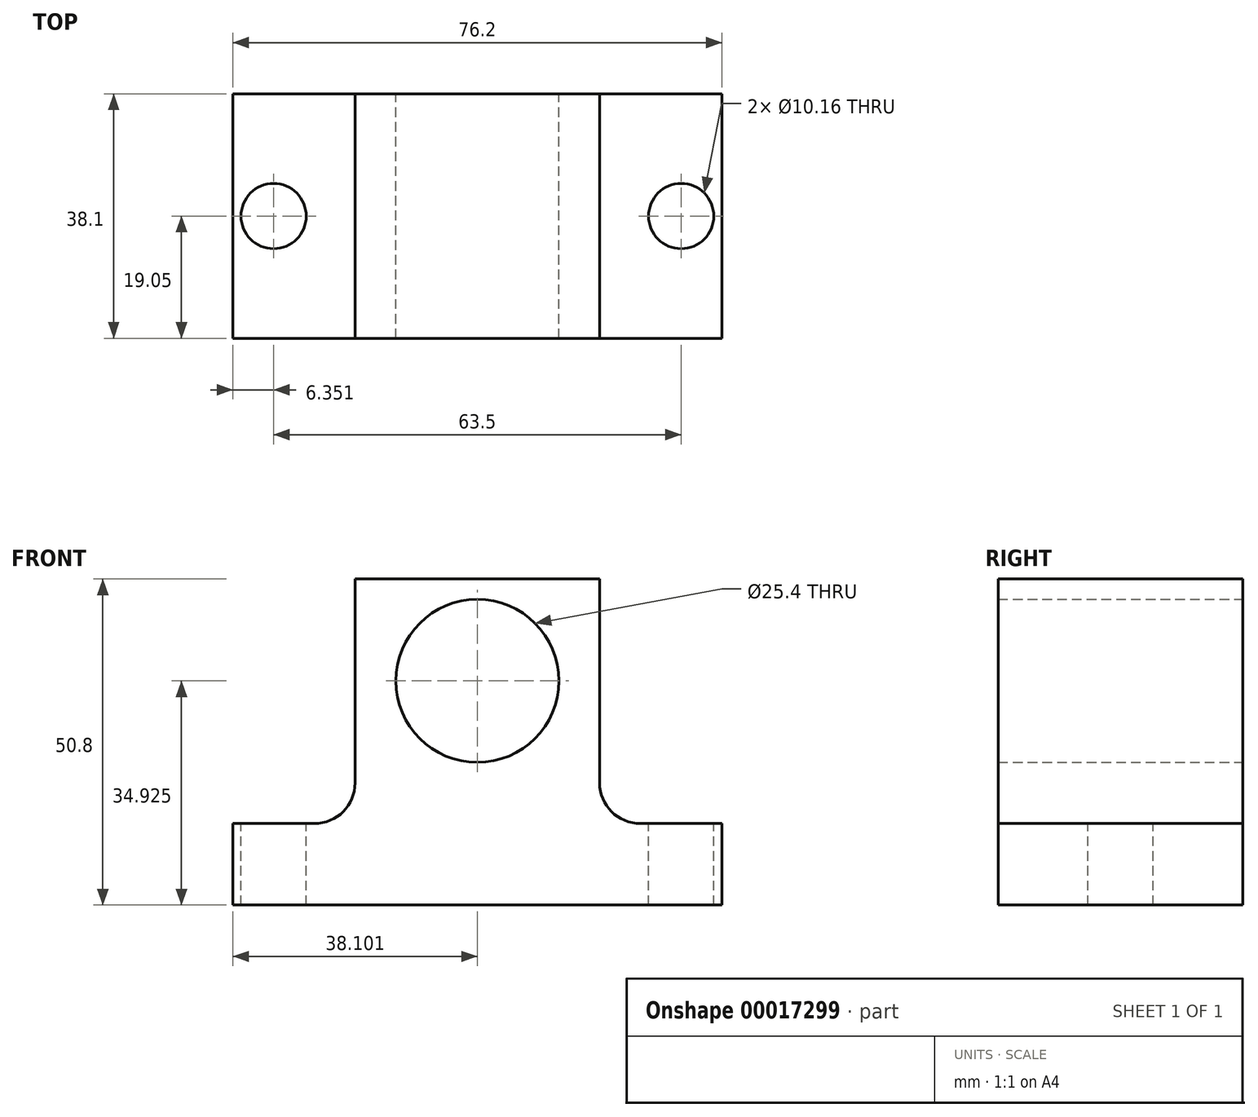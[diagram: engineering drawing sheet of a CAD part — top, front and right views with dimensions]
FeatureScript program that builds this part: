
annotation { "Feature Type Name" : "Feature", "Feature Type Description" : "" }
export const myFeature = defineFeature(function(context is Context, id is Id, definition is map)
    precondition{}
    {
        {
            var Q0;
            Q0=qCreatedBy(makeId("Front.planeOp"),FACE);
            var sketch = newSketch(context, id + "F0", { "sketchPlane" : qUnion([Q0])});
            skLineSegment(sketch, "E0", {"start": v(-55.57, 0) * mm, "end": v(-55.57, -12.7) * mm});
            skLineSegment(sketch, "E1", {"start": v(1.58, 6.35) * mm, "end": v(1.58, 38.1) * mm});
            skLineSegment(sketch, "E2", {"start": v(1.58, 38.1) * mm, "end": v(-36.52, 38.1) * mm});
            skLineSegment(sketch, "E3", {"start": v(20.63, 0) * mm, "end": v(20.63, -12.7) * mm});
            skLineSegment(sketch, "E4", {"start": v(7.93, 0) * mm, "end": v(20.63, 0) * mm});
            skLineSegment(sketch, "E5", {"start": v(20.63, -12.7) * mm, "end": v(-55.57, -12.7) * mm});
            skPoint(sketch, "E6.visualSharp", {"position": v(1.58, 0) * mm});
            skArc(sketch, "E6.filletArc", {"start": v(1.58, 6.35) * mm, "mid": v(3.44, 1.86) * mm, "end": v(7.93, 0) * mm});
            skLineSegment(sketch, "E7", {"start": v(-36.52, 38.1) * mm, "end": v(-36.52, 6.35) * mm});
            skLineSegment(sketch, "E8", {"start": v(-55.57, 0) * mm, "end": v(-42.87, 0) * mm});
            skPoint(sketch, "E9.visualSharp", {"position": v(-36.52, 0) * mm});
            skArc(sketch, "E9.filletArc", {"start": v(-42.87, 0) * mm, "mid": v(-38.38, 1.86) * mm, "end": v(-36.52, 6.35) * mm});
            skCircle(sketch, "E10", {"center": v(-17.47, 22.23) * mm, "radius": 12.7 * mm});
            skSolve(sketch);
        }
        {
            var Q0;
            Q0=makeQuery(id+"F0.imprint","IMPRINT",FACE,{"disambiguationData":[TD([[makeQuery(id+"F0.imprint","IMPRINT",EDGE,{"derivedFrom":sQuery(id+"F0.wireOp",EDGE,"E0")}),1.0]])]});
            var sketch = newSketch(context, id + "F1", { "sketchPlane" : qUnion([Q0])});
            skSolve(sketch);
        }
        {
            var Q0;
            Q0 = qSketchRegion(id + "F1", true);
            var Q1;
            Q1=makeQuery(id+"F0.imprint","IMPRINT",FACE,{"disambiguationData":[TD([[makeQuery(id+"F0.imprint","IMPRINT",EDGE,{"derivedFrom":sQuery(id+"F0.wireOp",EDGE,"E0")}),1.0]])]});
            extrude(context, id + "F2", {"entities" : qUnion([Q0, Q1]), "depth" : 38.1 * mm});
        }
        {
            var Q0;
            Q0=makeQuery(id+"F2.opExtrude","SWEPT_FACE",FACE,{"disambiguationData":[OSD([sQuery(id+"F0.wireOp",EDGE,"E8")])]});
            var sketch = newSketch(context, id + "F3", { "sketchPlane" : qUnion([Q0])});
            skCircle(sketch, "E11", {"center": v(-49.22, -19.05) * mm, "radius": 5.08 * mm});
            skSolve(sketch);
        }
        {
            var Q0;
            Q0=makeQuery(id+"F3.imprint","IMPRINT",FACE,{"disambiguationData":[TD([[makeQuery(id+"F3.imprint","IMPRINT",EDGE,{"derivedFrom":sQuery(id+"F3.wireOp",EDGE,"E11")}),1.0]])]});
            extrude(context, id + "F4", {"entities" : qUnion([Q0]), "operationType" : NewBodyOperationType.REMOVE, "endBound" : BoundingType.THROUGH_ALL, "oppositeDirection" : true, "depth" : 25.4 * mm});
        }
        {
            var Q0;
            Q0=makeQuery(id+"F2.opExtrude","SWEPT_FACE",FACE,{"disambiguationData":[OSD([sQuery(id+"F0.wireOp",EDGE,"E4")])]});
            var sketch = newSketch(context, id + "F5", { "sketchPlane" : qUnion([Q0])});
            skCircle(sketch, "E12", {"center": v(14.28, -19.05) * mm, "radius": 5.08 * mm});
            skSolve(sketch);
        }
        {
            var Q0;
            Q0=makeQuery(id+"F5.imprint","IMPRINT",FACE,{"disambiguationData":[TD([[makeQuery(id+"F5.imprint","IMPRINT",EDGE,{"derivedFrom":sQuery(id+"F5.wireOp",EDGE,"E12")}),1.0]])]});
            extrude(context, id + "F6", {"entities" : qUnion([Q0]), "operationType" : NewBodyOperationType.REMOVE, "endBound" : BoundingType.THROUGH_ALL, "oppositeDirection" : true, "depth" : 25.4 * mm});
        }
    });
